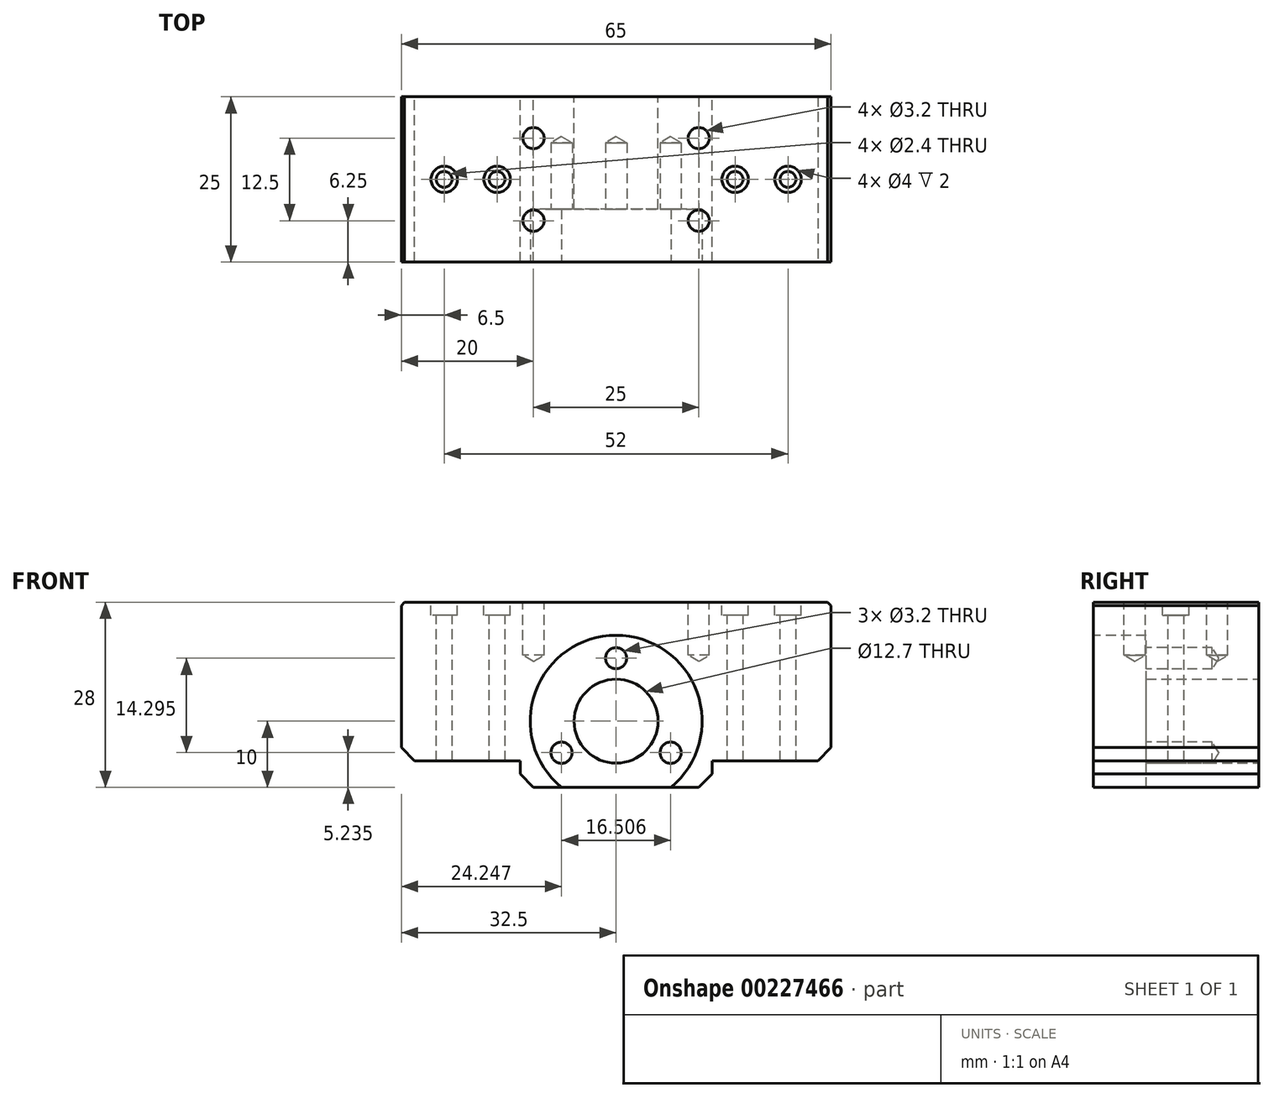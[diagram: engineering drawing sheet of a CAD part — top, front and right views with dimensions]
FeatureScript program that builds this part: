
annotation { "Feature Type Name" : "Feature", "Feature Type Description" : "" }
export const myFeature = defineFeature(function(context is Context, id is Id, definition is map)
    precondition{}
    {
        {
            var Q0;
            Q0=qCreatedBy(makeId("Front.planeOp"),FACE);
            var sketch = newSketch(context, id + "F0", { "sketchPlane" : qUnion([Q0])});
            skLineSegment(sketch, "E0.bottom", {"start": v(32.5, -10) * mm, "end": v(-32.5, -10) * mm});
            skLineSegment(sketch, "E0.top", {"start": v(32.5, 18) * mm, "end": v(-32.5, 18) * mm});
            skLineSegment(sketch, "E0.left", {"start": v(32.5, -10) * mm, "end": v(32.5, 18) * mm});
            skLineSegment(sketch, "E0.right", {"start": v(-32.5, -10) * mm, "end": v(-32.5, 18) * mm});
            skPoint(sketch, "E0.middle", {"position": v(0, 0) * mm});
            skCircle(sketch, "E1", {"center": v(0, 0) * mm, "radius": 6.35 * mm});
            skPoint(sketch, "E2", {"position": v(0, -10) * mm});
            skPoint(sketch, "E3", {"position": v(32.5, -6) * mm});
            skLineSegment(sketch, "E4", {"start": v(32.5, -6) * mm, "end": v(14.5, -6) * mm});
            skLineSegment(sketch, "E5", {"start": v(14.5, -6) * mm, "end": v(14.5, -10) * mm});
            skLineSegment(sketch, "E6.MirrorCS", {"start": v(-32.5, -6) * mm, "end": v(-14.5, -6) * mm});
            skLineSegment(sketch, "E7.MirrorCS", {"start": v(-14.5, -6) * mm, "end": v(-14.5, -10) * mm});
            skSolve(sketch);
        }
        {
            var Q0;
            {var subQ1=sQuery(id+"F0.wireOp",EDGE,"E0.top");Q0=makeQuery(id+"F0.imprint","IMPRINT",FACE,{"disambiguationData":[TD([[makeQuery(id+"F0.imprint","IMPRINT",EDGE,{"derivedFrom":subQ1}),1.0]])]});}
            extrude(context, id + "F1", {"entities" : qUnion([Q0]), "depth" : 25 * mm});
        }
        {
            var Q0;
            Q0=makeQuery(id+"F1.opExtrude","SWEPT_EDGE",EDGE,{"disambiguationData":[OSD([sQuery(id+"F0.wireOp",EDGE,"E0.top"),sQuery(id+"F0.wireOp",EDGE,"E0.right")])]});
            var Q1;
            Q1=makeQuery(id+"F1.opExtrude","SWEPT_EDGE",EDGE,{"disambiguationData":[OSD([sQuery(id+"F0.wireOp",EDGE,"E0.top"),sQuery(id+"F0.wireOp",EDGE,"E0.left")])]});
            chamfer(context, id + "F2", {"entities" : qUnion([Q0, Q1]), "width" : 0.5 * mm, "tangentPropagation" : true});
        }
        {
            var Q0;
            Q0=makeQuery(id+"F1.opExtrude","CAP_FACE",FACE,{"disambiguationData":[OSD([sQuery(id+"F0.wireOp",EDGE,"E0.bottom"),sQuery(id+"F0.wireOp",EDGE,"E0.top"),sQuery(id+"F0.wireOp",EDGE,"E0.left"),sQuery(id+"F0.wireOp",EDGE,"E0.right"),sQuery(id+"F0.wireOp",EDGE,"E1")])],"isStart":false});
            var sketch = newSketch(context, id + "F3", { "sketchPlane" : qUnion([Q0])});
            skCircle(sketch, "E8", {"center": v(0, 0) * mm, "radius": 13 * mm});
            skSolve(sketch);
        }
        {
            var Q0;
            Q0=makeQuery(id+"F3.imprint","IMPRINT",FACE,{"disambiguationData":[TD([[makeQuery(id+"F3.imprint","IMPRINT",EDGE,{"derivedFrom":makeQuery(id+"F1.opExtrude","CAP_EDGE",EDGE,{"disambiguationData":[OSD([sQuery(id+"F0.wireOp",EDGE,"E1")])],"isStart":false})}),-1.0]])]});
            extrude(context, id + "F4", {"entities" : qUnion([Q0]), "operationType" : NewBodyOperationType.REMOVE, "oppositeDirection" : true, "depth" : 8 * mm});
        }
        {
            var Q0;
            Q0=makeQuery(id+"F1.opExtrude","SWEPT_EDGE",EDGE,{"disambiguationData":[OSD([sQuery(id+"F0.wireOp",EDGE,"E0.bottom"),sQuery(id+"F0.wireOp",EDGE,"E0.left")])]});
            var Q1;
            Q1=makeQuery(id+"F1.opExtrude","SWEPT_EDGE",EDGE,{"disambiguationData":[OSD([sQuery(id+"F0.wireOp",EDGE,"E0.bottom"),sQuery(id+"F0.wireOp",EDGE,"E0.right")])]});
            chamfer(context, id + "F5", {"entities" : qUnion([Q0, Q1]), "width" : 2 * mm, "tangentPropagation" : true});
        }
        {
            var Q0;
            Q0=makeQuery(id+"F1.opExtrude","SWEPT_FACE",FACE,{"disambiguationData":[OSD([sQuery(id+"F0.wireOp",EDGE,"E0.top")])]});
            var sketch = newSketch(context, id + "F6", { "sketchPlane" : qUnion([Q0])});
            skPoint(sketch, "E9", {"position": v(12.5, -6.25) * mm});
            skPoint(sketch, "E10.0.1.0", {"position": v(12.5, -18.75) * mm});
            skPoint(sketch, "E10.1.0.0", {"position": v(-12.5, -6.25) * mm});
            skPoint(sketch, "E10.1.1.0", {"position": v(-12.5, -18.75) * mm});
            skLineSegment(sketch, "E10.direction1", {"start": v(12.5, -6.25) * mm, "end": v(-12.5, -6.25) * mm, "construction": true});
            skLineSegment(sketch, "E10.direction2", {"start": v(12.5, -6.25) * mm, "end": v(12.5, -18.75) * mm, "construction": true});
            skSolve(sketch);
        }
        {
            var Q0;
            Q0=sQuery(id+"F6.wireOp",VERTEX,"E9");
            var Q1;
            Q1=sQuery(id+"F6.wireOp",VERTEX,"E10.0.1.0");
            var Q2;
            Q2=sQuery(id+"F6.wireOp",VERTEX,"E10.1.0.0");
            var Q3;
            Q3=sQuery(id+"F6.wireOp",VERTEX,"E10.1.1.0");
            var Q4;
            Q4=makeQuery(id+"F1.opExtrude","SWEPT_BODY",BODY,{"disambiguationData":[OSD([sQuery(id+"F0.wireOp",EDGE,"E0.bottom"),sQuery(id+"F0.wireOp",EDGE,"E0.top"),sQuery(id+"F0.wireOp",EDGE,"E0.left"),sQuery(id+"F0.wireOp",EDGE,"E0.right"),sQuery(id+"F0.wireOp",EDGE,"E1")])]});
            hole(context, id + "F7", {"style" : HoleStyle.SIMPLE, "endStyle" : HoleEndStyle.BLIND, "standardTappedOrClearance" : lookupTablePath({ "standard" : "ISO", "engagement" : "75%", "pitch" : "0.75 mm", "size" : "M4", "type" : "Tapped" }), "standardBlindInLast" : lookupTablePath({ "standard" : "ISO", "engagement" : "75%", "pitch" : "0.75 mm", "size" : "M4", "type" : "Tapped" }), "holeDiameter" : 3.2 * mm, "holeDepth" : 8 * mm, "locations" : qUnion([Q0, Q1, Q2, Q3]), "scope" : qUnion([Q4])});
        }
        {
            var Q0;
            Q0=makeQuery(id+"F1.opExtrude","SWEPT_FACE",FACE,{"disambiguationData":[OSD([sQuery(id+"F0.wireOp",EDGE,"E0.top")])]});
            var sketch = newSketch(context, id + "F8", { "sketchPlane" : qUnion([Q0])});
            skPoint(sketch, "E11", {"position": v(-26, -12.5) * mm});
            skPoint(sketch, "E12.1.0.0", {"position": v(-18, -12.5) * mm});
            skLineSegment(sketch, "E12.direction1", {"start": v(-26, -12.5) * mm, "end": v(-18, -12.5) * mm, "construction": true});
            skLineSegment(sketch, "E12.direction2", {"start": v(-26, -12.5) * mm, "end": v(-26, -22.5) * mm, "construction": true});
            skPoint(sketch, "E13.MirrorP", {"position": v(26, -12.5) * mm});
            skPoint(sketch, "E14.MirrorP", {"position": v(18, -12.5) * mm});
            skSolve(sketch);
        }
        {
            var Q0;
            Q0=sQuery(id+"F8.wireOp",VERTEX,"E11");
            var Q1;
            Q1=sQuery(id+"F8.wireOp",VERTEX,"E12.1.0.0");
            var Q2;
            Q2=sQuery(id+"F8.wireOp",VERTEX,"E14.MirrorP");
            var Q3;
            Q3=sQuery(id+"F8.wireOp",VERTEX,"E13.MirrorP");
            var Q4;
            Q4=makeQuery(id+"F1.opExtrude","SWEPT_BODY",BODY,{"disambiguationData":[OSD([sQuery(id+"F0.wireOp",EDGE,"E0.bottom"),sQuery(id+"F0.wireOp",EDGE,"E0.top"),sQuery(id+"F0.wireOp",EDGE,"E0.left"),sQuery(id+"F0.wireOp",EDGE,"E0.right"),sQuery(id+"F0.wireOp",EDGE,"E1")])]});
            hole(context, id + "F9", {"style" : HoleStyle.C_BORE, "endStyle" : HoleEndStyle.THROUGH, "holeDiameter" : 2.4 * mm, "cBoreDiameter" : 4 * mm, "cBoreDepth" : 2 * mm, "locations" : qUnion([Q0, Q1, Q2, Q3]), "scope" : qUnion([Q4]), "isTappedThrough" : true});
        }
        {
            var Q0;
            Q0=makeQuery(id+"F4.boolean.opBoolean","COPY",FACE,{"derivedFrom":makeQuery(id+"F4.opExtrude","CAP_FACE",FACE,{"disambiguationData":[OSD([sQuery(id+"F0.wireOp",EDGE,"E0.bottom"),sQuery(id+"F0.wireOp",EDGE,"E1"),sQuery(id+"F3.wireOp",EDGE,"E8")])],"isStart":false})});
            var sketch = newSketch(context, id + "F10", { "sketchPlane" : qUnion([Q0])});
            skCircle(sketch, "E15", {"center": v(0, 0) * mm, "radius": 9.53 * mm, "construction": true});
            skPoint(sketch, "E16", {"position": v(0, 9.53) * mm});
            skPoint(sketch, "E17.1.0", {"position": v(-8.25, -4.76) * mm});
            skPoint(sketch, "E17.2.0", {"position": v(8.25, -4.77) * mm});
            skSolve(sketch);
        }
        {
            var Q0;
            Q0=sQuery(id+"F10.wireOp",VERTEX,"E16");
            var Q1;
            Q1=sQuery(id+"F10.wireOp",VERTEX,"E17.2.0");
            var Q2;
            Q2=sQuery(id+"F10.wireOp",VERTEX,"E17.1.0");
            var Q3;
            Q3=makeQuery(id+"F1.opExtrude","SWEPT_BODY",BODY,{"disambiguationData":[OSD([sQuery(id+"F0.wireOp",EDGE,"E0.bottom"),sQuery(id+"F0.wireOp",EDGE,"E0.top"),sQuery(id+"F0.wireOp",EDGE,"E0.left"),sQuery(id+"F0.wireOp",EDGE,"E0.right"),sQuery(id+"F0.wireOp",EDGE,"E1")])]});
            hole(context, id + "F11", {"style" : HoleStyle.SIMPLE, "endStyle" : HoleEndStyle.BLIND, "standardTappedOrClearance" : lookupTablePath({ "standard" : "ISO", "engagement" : "75%", "pitch" : "0.75 mm", "size" : "M4", "type" : "Tapped" }), "standardBlindInLast" : lookupTablePath({ "standard" : "ISO", "engagement" : "75%", "pitch" : "0.75 mm", "size" : "M4", "type" : "Tapped" }), "holeDiameter" : 3.2 * mm, "holeDepth" : 10 * mm, "locations" : qUnion([Q0, Q1, Q2]), "scope" : qUnion([Q3])});
        }
    });
